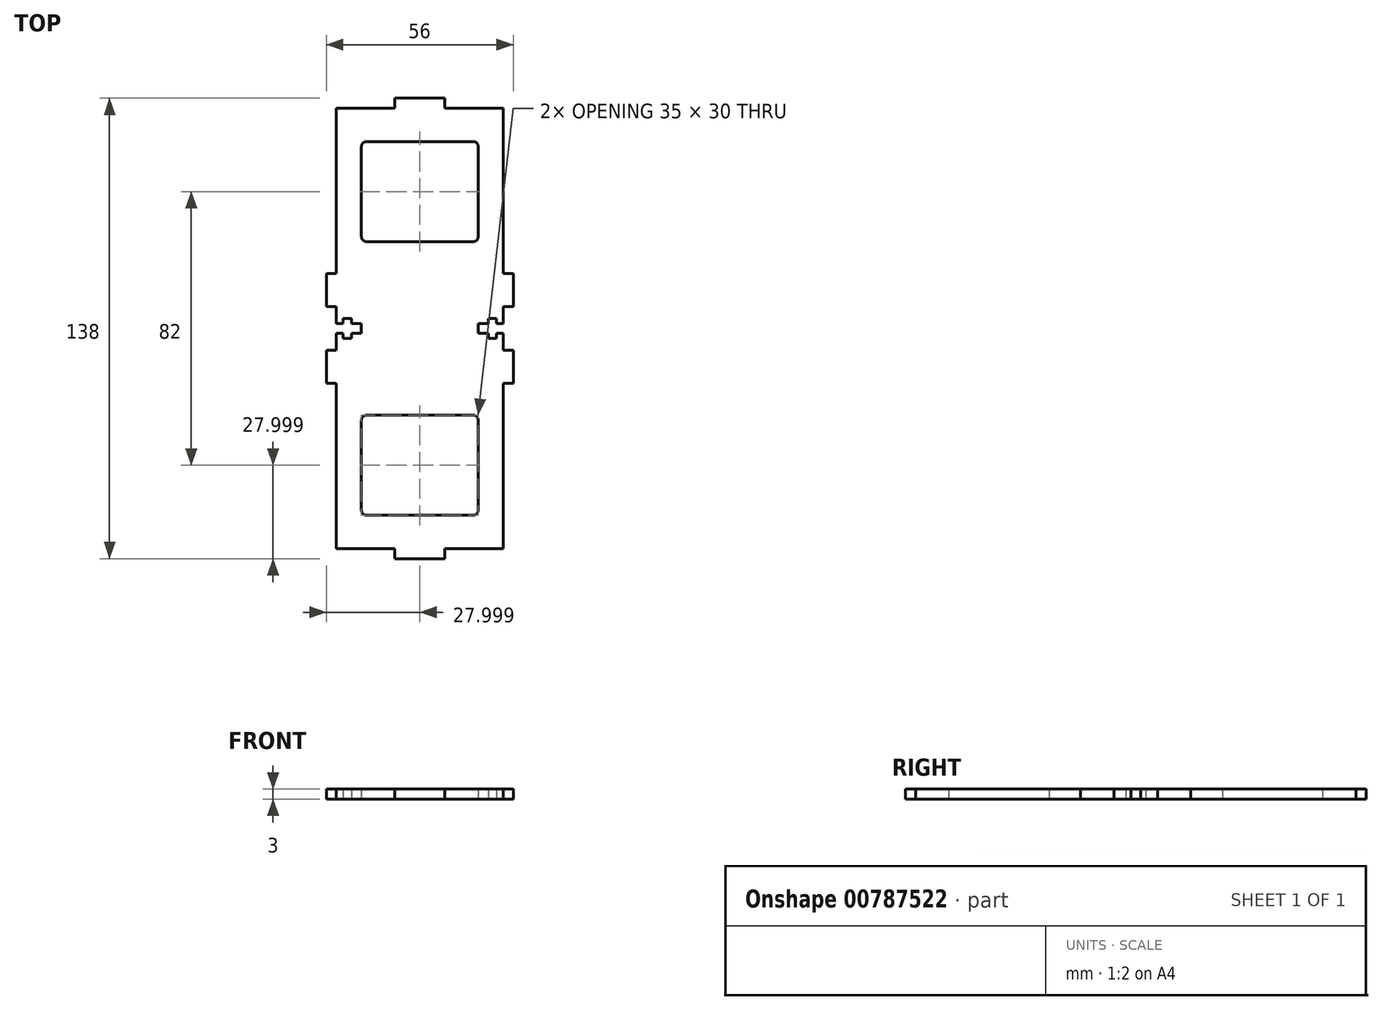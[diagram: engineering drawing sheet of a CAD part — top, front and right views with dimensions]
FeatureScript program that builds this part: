
annotation { "Feature Type Name" : "Feature", "Feature Type Description" : "" }
export const myFeature = defineFeature(function(context is Context, id is Id, definition is map)
    precondition{}
    {
        {
            var Q0;
            Q0=qCreatedBy(makeId("Top.planeOp"),FACE);
            var sketch = newSketch(context, id + "F0", { "sketchPlane" : qUnion([Q0])});
            skLineSegment(sketch, "E0.bottom", {"start": v(-34.93, 10.96) * mm, "end": v(-52.43, 10.96) * mm});
            skLineSegment(sketch, "E0.top", {"start": v(-34.93, -121.04) * mm, "end": v(-52.43, -121.04) * mm});
            skLineSegment(sketch, "E0.left", {"start": v(-34.93, 10.96) * mm, "end": v(-34.93, -38.54) * mm});
            skLineSegment(sketch, "E0.right", {"start": v(-84.93, 10.96) * mm, "end": v(-84.93, -38.54) * mm});
            skLineSegment(sketch, "E1.bottom", {"start": v(-67.43, 13.96) * mm, "end": v(-52.43, 13.96) * mm});
            skLineSegment(sketch, "E1.left", {"start": v(-67.43, 13.96) * mm, "end": v(-67.43, 10.96) * mm});
            skLineSegment(sketch, "E1.right", {"start": v(-52.43, 13.96) * mm, "end": v(-52.43, 10.96) * mm});
            skPoint(sketch, "E1.middle", {"position": v(-59.93, 10.96) * mm});
            skLineSegment(sketch, "E2.top", {"start": v(-67.43, -124.04) * mm, "end": v(-52.43, -124.04) * mm});
            skLineSegment(sketch, "E2.left", {"start": v(-67.43, -121.04) * mm, "end": v(-67.43, -124.04) * mm});
            skLineSegment(sketch, "E2.right", {"start": v(-52.43, -121.04) * mm, "end": v(-52.43, -124.04) * mm});
            skLineSegment(sketch, "E3.trimOffspring", {"start": v(-67.43, -121.04) * mm, "end": v(-84.93, -121.04) * mm});
            skLineSegment(sketch, "E4.trimOffspring", {"start": v(-67.43, 10.96) * mm, "end": v(-84.93, 10.96) * mm});
            skLineSegment(sketch, "E5", {"start": v(-84.93, -55.04) * mm, "end": v(-34.93, -55.04) * mm, "construction": true});
            skLineSegment(sketch, "E6", {"start": v(-84.93, -53.54) * mm, "end": v(-82.93, -53.54) * mm});
            skLineSegment(sketch, "E7", {"start": v(-82.93, -53.54) * mm, "end": v(-82.93, -52.04) * mm});
            skLineSegment(sketch, "E8", {"start": v(-82.93, -52.04) * mm, "end": v(-80.43, -52.04) * mm});
            skLineSegment(sketch, "E9", {"start": v(-80.43, -52.04) * mm, "end": v(-80.43, -53.54) * mm});
            skLineSegment(sketch, "E10", {"start": v(-80.43, -53.54) * mm, "end": v(-77.43, -53.54) * mm});
            skLineSegment(sketch, "E11", {"start": v(-77.43, -53.54) * mm, "end": v(-77.43, -56.54) * mm});
            skLineSegment(sketch, "E12", {"start": v(-77.43, -56.54) * mm, "end": v(-80.43, -56.54) * mm});
            skLineSegment(sketch, "E13", {"start": v(-80.43, -56.54) * mm, "end": v(-80.43, -58.04) * mm});
            skLineSegment(sketch, "E14", {"start": v(-80.43, -58.04) * mm, "end": v(-82.93, -58.04) * mm});
            skLineSegment(sketch, "E15", {"start": v(-82.93, -58.04) * mm, "end": v(-82.93, -56.54) * mm});
            skLineSegment(sketch, "E16", {"start": v(-82.93, -56.54) * mm, "end": v(-84.93, -56.54) * mm});
            skLineSegment(sketch, "E17", {"start": v(-84.93, -48.54) * mm, "end": v(-87.93, -48.54) * mm});
            skLineSegment(sketch, "E18", {"start": v(-87.93, -48.54) * mm, "end": v(-87.93, -38.54) * mm});
            skLineSegment(sketch, "E19", {"start": v(-87.93, -38.54) * mm, "end": v(-84.93, -38.54) * mm});
            skLineSegment(sketch, "E20", {"start": v(-84.93, -61.54) * mm, "end": v(-87.93, -61.54) * mm});
            skLineSegment(sketch, "E21", {"start": v(-87.93, -61.54) * mm, "end": v(-87.93, -71.54) * mm});
            skLineSegment(sketch, "E22", {"start": v(-87.93, -71.54) * mm, "end": v(-84.93, -71.54) * mm});
            skLineSegment(sketch, "E23.trimOffspring", {"start": v(-84.93, -48.54) * mm, "end": v(-84.93, -53.54) * mm});
            skLineSegment(sketch, "E24.trimOffspring", {"start": v(-84.93, -71.54) * mm, "end": v(-84.93, -121.04) * mm});
            skLineSegment(sketch, "E25.trimOffspring", {"start": v(-84.93, -56.54) * mm, "end": v(-84.93, -61.54) * mm});
            skLineSegment(sketch, "E26", {"start": v(-34.93, -56.54) * mm, "end": v(-36.93, -56.54) * mm});
            skLineSegment(sketch, "E27", {"start": v(-36.93, -56.54) * mm, "end": v(-36.93, -58.04) * mm});
            skLineSegment(sketch, "E28", {"start": v(-36.93, -58.04) * mm, "end": v(-39.43, -58.04) * mm});
            skLineSegment(sketch, "E29", {"start": v(-39.43, -58.04) * mm, "end": v(-39.43, -56.54) * mm});
            skLineSegment(sketch, "E30", {"start": v(-39.43, -56.54) * mm, "end": v(-42.43, -56.54) * mm});
            skLineSegment(sketch, "E31", {"start": v(-42.43, -56.54) * mm, "end": v(-42.43, -53.54) * mm});
            skLineSegment(sketch, "E32", {"start": v(-42.43, -53.54) * mm, "end": v(-39.43, -53.54) * mm});
            skLineSegment(sketch, "E33", {"start": v(-39.43, -53.54) * mm, "end": v(-39.43, -52.04) * mm});
            skLineSegment(sketch, "E34", {"start": v(-39.43, -52.04) * mm, "end": v(-36.93, -52.04) * mm});
            skLineSegment(sketch, "E35", {"start": v(-36.93, -52.04) * mm, "end": v(-36.93, -53.54) * mm});
            skLineSegment(sketch, "E36", {"start": v(-36.93, -53.54) * mm, "end": v(-34.93, -53.54) * mm});
            skLineSegment(sketch, "E37", {"start": v(-34.93, -61.54) * mm, "end": v(-31.93, -61.54) * mm});
            skLineSegment(sketch, "E38", {"start": v(-31.93, -61.54) * mm, "end": v(-31.93, -71.54) * mm});
            skLineSegment(sketch, "E39", {"start": v(-31.93, -71.54) * mm, "end": v(-34.93, -71.54) * mm});
            skLineSegment(sketch, "E40", {"start": v(-34.93, -48.54) * mm, "end": v(-31.93, -48.54) * mm});
            skLineSegment(sketch, "E41", {"start": v(-31.93, -48.54) * mm, "end": v(-31.93, -38.54) * mm});
            skLineSegment(sketch, "E42", {"start": v(-31.93, -38.54) * mm, "end": v(-34.93, -38.54) * mm});
            skLineSegment(sketch, "E43.trimOffspring", {"start": v(-34.93, -48.54) * mm, "end": v(-34.93, -53.54) * mm});
            skLineSegment(sketch, "E44.trimOffspring", {"start": v(-34.93, -71.54) * mm, "end": v(-34.93, -121.04) * mm});
            skLineSegment(sketch, "E45.trimOffspring", {"start": v(-34.93, -56.54) * mm, "end": v(-34.93, -61.54) * mm});
            skLineSegment(sketch, "E46.bottom", {"start": v(-75.93, 0.96) * mm, "end": v(-43.93, 0.96) * mm});
            skLineSegment(sketch, "E46.top", {"start": v(-75.93, -29.04) * mm, "end": v(-43.93, -29.04) * mm});
            skLineSegment(sketch, "E46.left", {"start": v(-77.43, -0.54) * mm, "end": v(-77.43, -27.54) * mm});
            skLineSegment(sketch, "E46.right", {"start": v(-42.43, -0.54) * mm, "end": v(-42.43, -27.54) * mm});
            skPoint(sketch, "E46.middle", {"position": v(-59.93, -14.04) * mm});
            skPoint(sketch, "E47.visualSharp", {"position": v(-77.43, 0.96) * mm});
            skArc(sketch, "E47.filletArc", {"start": v(-75.93, 0.96) * mm, "mid": v(-77, 0.52) * mm, "end": v(-77.43, -0.54) * mm});
            skPoint(sketch, "E48.visualSharp", {"position": v(-42.43, 0.96) * mm});
            skArc(sketch, "E48.filletArc", {"start": v(-42.43, -0.54) * mm, "mid": v(-42.87, 0.52) * mm, "end": v(-43.93, 0.96) * mm});
            skPoint(sketch, "E49.visualSharp", {"position": v(-42.43, -29.04) * mm});
            skArc(sketch, "E49.filletArc", {"start": v(-43.93, -29.04) * mm, "mid": v(-42.87, -28.6) * mm, "end": v(-42.43, -27.54) * mm});
            skPoint(sketch, "E50.visualSharp", {"position": v(-77.43, -29.04) * mm});
            skArc(sketch, "E50.filletArc", {"start": v(-77.43, -27.54) * mm, "mid": v(-77, -28.6) * mm, "end": v(-75.93, -29.04) * mm});
            skLineSegment(sketch, "E51", {"start": v(-42.43, -55.04) * mm, "end": v(-77.43, -55.04) * mm, "construction": true});
            skArc(sketch, "E52.MirrorCS", {"start": v(-43.93, -81.04) * mm, "mid": v(-42.87, -81.48) * mm, "end": v(-42.43, -82.54) * mm});
            skArc(sketch, "E53.MirrorCS", {"start": v(-77.43, -82.54) * mm, "mid": v(-77, -81.48) * mm, "end": v(-75.93, -81.04) * mm});
            skArc(sketch, "E54.MirrorCS", {"start": v(-75.93, -111.04) * mm, "mid": v(-77, -110.6) * mm, "end": v(-77.43, -109.54) * mm});
            skArc(sketch, "E55.MirrorCS", {"start": v(-42.43, -109.54) * mm, "mid": v(-42.87, -110.6) * mm, "end": v(-43.93, -111.04) * mm});
            skLineSegment(sketch, "E56.MirrorCS", {"start": v(-75.93, -111.04) * mm, "end": v(-43.93, -111.04) * mm});
            skLineSegment(sketch, "E57.MirrorCS", {"start": v(-77.43, -109.54) * mm, "end": v(-77.43, -82.54) * mm});
            skPoint(sketch, "E58.MirrorP", {"position": v(-77.43, -81.04) * mm});
            skLineSegment(sketch, "E59.MirrorCS", {"start": v(-75.93, -81.04) * mm, "end": v(-43.93, -81.04) * mm});
            skLineSegment(sketch, "E60.MirrorCS", {"start": v(-42.43, -109.54) * mm, "end": v(-42.43, -82.54) * mm});
            skPoint(sketch, "E61.MirrorP", {"position": v(-77.43, -111.04) * mm});
            skPoint(sketch, "E62.MirrorP", {"position": v(-42.43, -111.04) * mm});
            skPoint(sketch, "E63.MirrorP", {"position": v(-59.93, -96.04) * mm});
            skPoint(sketch, "E64.MirrorP", {"position": v(-42.43, -81.04) * mm});
            skSolve(sketch);
        }
        {
            var Q0;
            Q0=makeQuery(id+"F0.imprint","IMPRINT",FACE,{"disambiguationData":[TD([[makeQuery(id+"F0.imprint","IMPRINT",EDGE,{"derivedFrom":sQuery(id+"F0.wireOp",EDGE,"E0.bottom")}),1.0]])]});
            extrude(context, id + "F1", {"entities" : qUnion([Q0]), "depth" : 3 * mm, "offsetDistance" : 25.4 * mm});
        }
    });
